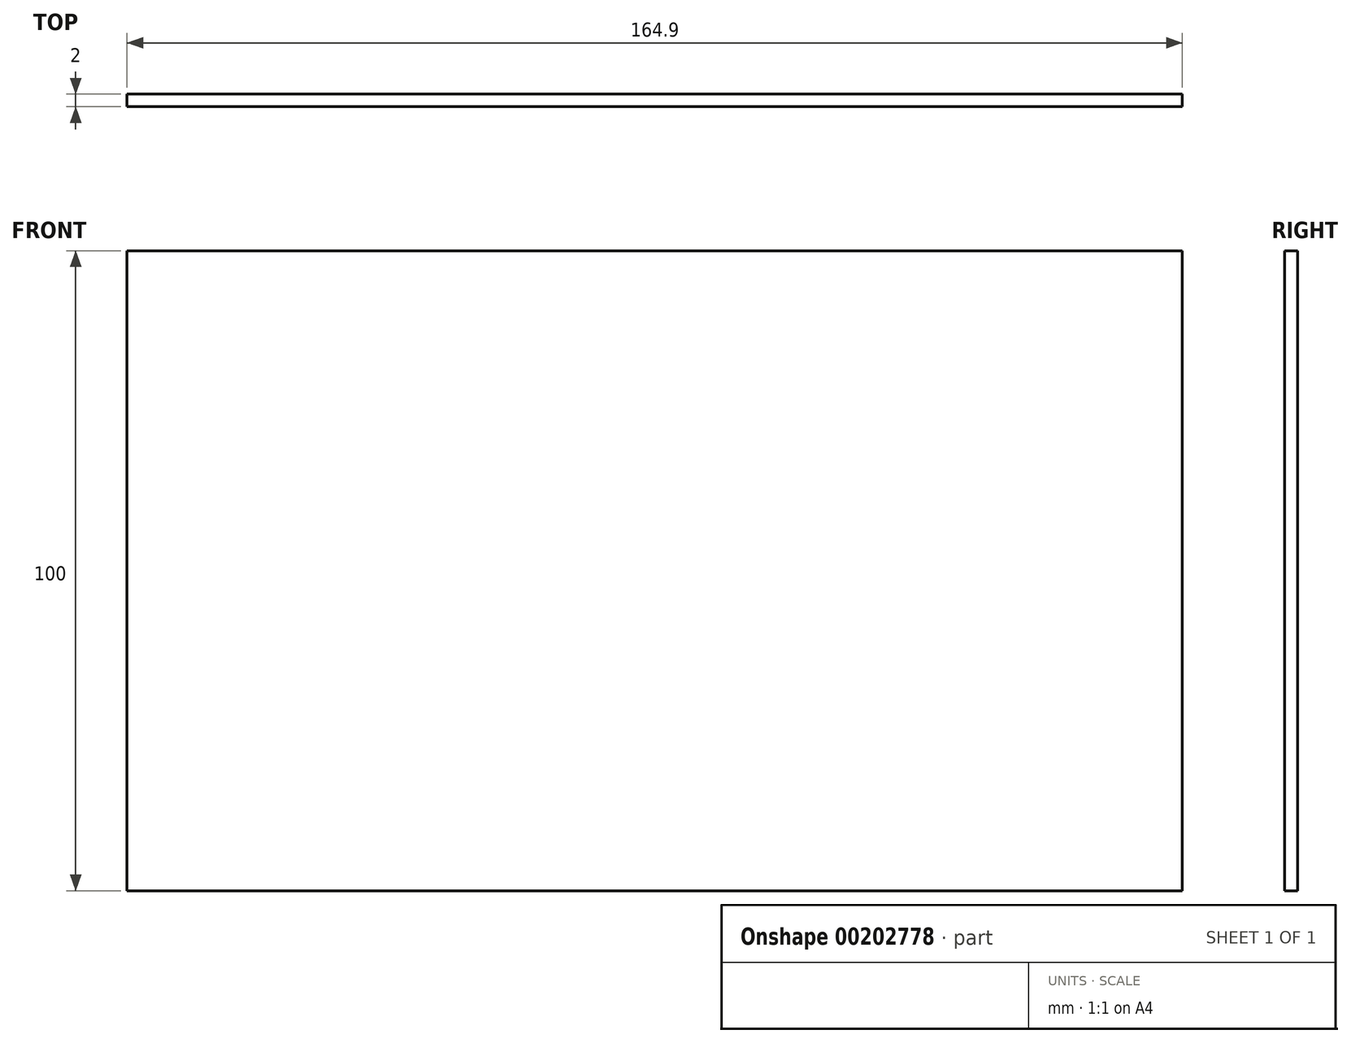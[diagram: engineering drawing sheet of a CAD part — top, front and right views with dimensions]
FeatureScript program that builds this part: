
annotation { "Feature Type Name" : "Feature", "Feature Type Description" : "" }
export const myFeature = defineFeature(function(context is Context, id is Id, definition is map)
    precondition{}
    {
        {
            var Q0;
            Q0=qCreatedBy(makeId("Front.planeOp"),FACE);
            var sketch = newSketch(context, id + "F0", { "sketchPlane" : qUnion([Q0])});
            skLineSegment(sketch, "E0.bottom", {"start": v(82.45, -50) * mm, "end": v(-82.45, -50) * mm});
            skLineSegment(sketch, "E0.top", {"start": v(82.45, 50) * mm, "end": v(-82.45, 50) * mm});
            skLineSegment(sketch, "E0.left", {"start": v(82.45, -50) * mm, "end": v(82.45, 50) * mm});
            skLineSegment(sketch, "E0.right", {"start": v(-82.45, -50) * mm, "end": v(-82.45, 50) * mm});
            skPoint(sketch, "E0.middle", {"position": v(0, 0) * mm});
            skSolve(sketch);
        }
        {
            var Q0;
            Q0=makeQuery(id+"F0.imprint","IMPRINT",FACE,{"disambiguationData":[TD([[makeQuery(id+"F0.imprint","IMPRINT",EDGE,{"derivedFrom":sQuery(id+"F0.wireOp",EDGE,"E0.bottom")}),-1.0]])]});
            extrude(context, id + "F1", {"entities" : qUnion([Q0]), "depth" : 2 * mm});
        }
    });
